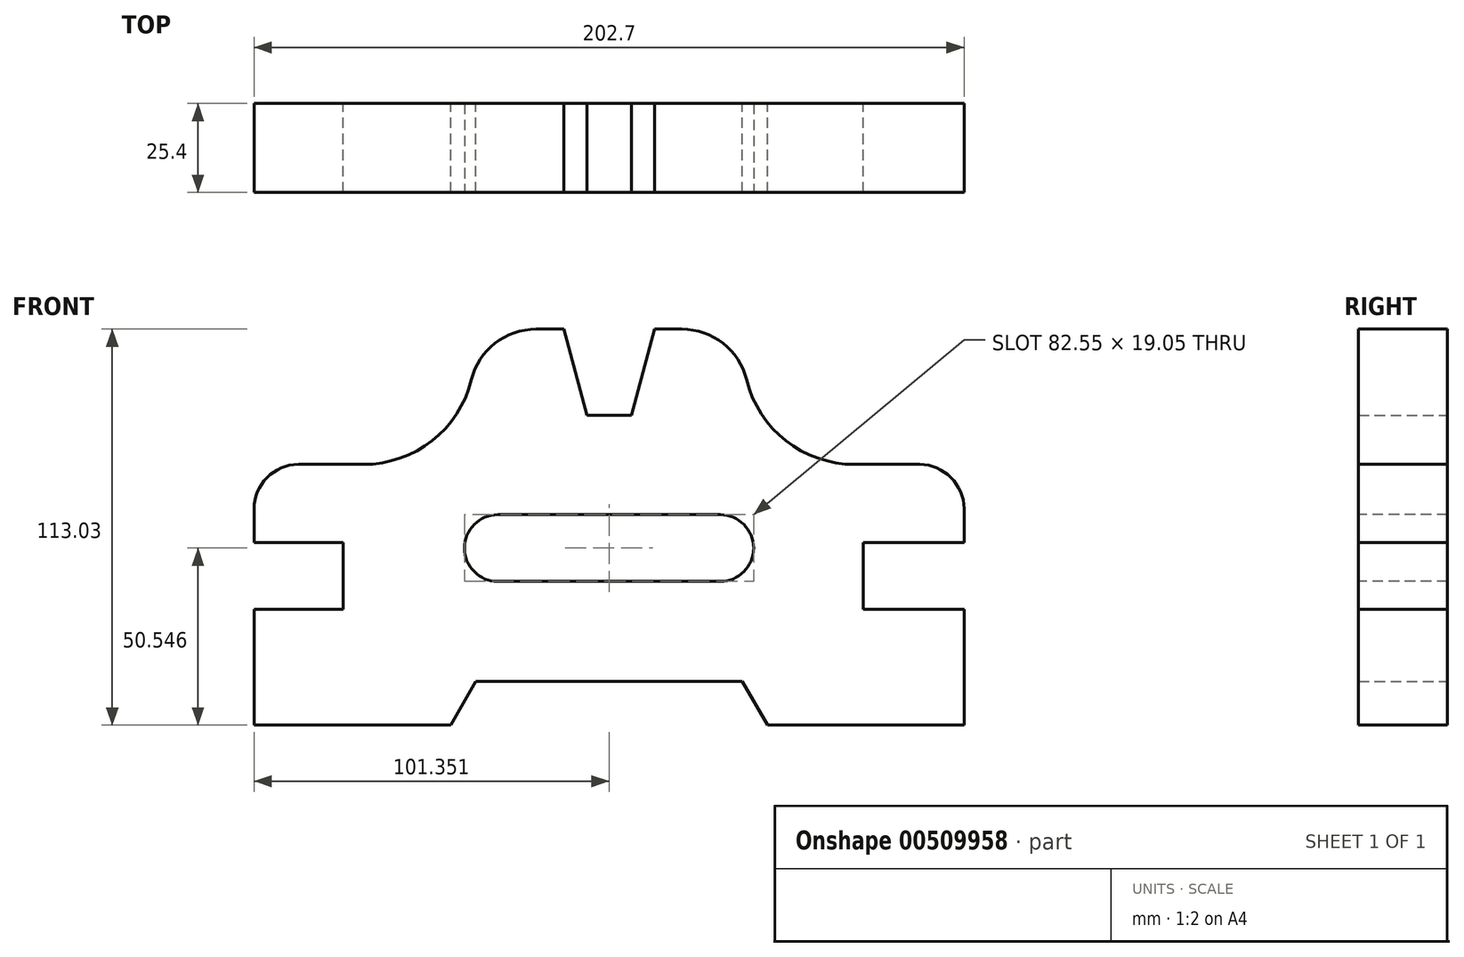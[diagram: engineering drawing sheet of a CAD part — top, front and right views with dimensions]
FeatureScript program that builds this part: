
annotation { "Feature Type Name" : "Feature", "Feature Type Description" : "" }
export const myFeature = defineFeature(function(context is Context, id is Id, definition is map)
    precondition{}
    {
        {
            var Q0;
            Q0=qCreatedBy(makeId("Front.planeOp"),FACE);
            var sketch = newSketch(context, id + "F0", { "sketchPlane" : qUnion([Q0])});
            skLineSegment(sketch, "E0", {"start": v(60.53, 19.05) * mm, "end": v(60.53, 0) * mm});
            skLineSegment(sketch, "E1", {"start": v(60.53, 0) * mm, "end": v(89.27, 0) * mm});
            skLineSegment(sketch, "E2", {"start": v(25.95, -20.57) * mm, "end": v(-50.1, -20.57) * mm});
            skLineSegment(sketch, "E3", {"start": v(-50.1, -20.57) * mm, "end": v(-57.3, -33.02) * mm});
            skLineSegment(sketch, "E4", {"start": v(-57.3, -33.02) * mm, "end": v(-113.43, -33.02) * mm});
            skLineSegment(sketch, "E5", {"start": v(-113.43, -33.02) * mm, "end": v(-113.43, 0) * mm});
            skLineSegment(sketch, "E6", {"start": v(-113.43, 0) * mm, "end": v(-113.43, 0) * mm});
            skLineSegment(sketch, "E7", {"start": v(-88.03, 19.05) * mm, "end": v(-113.43, 19.05) * mm});
            skLineSegment(sketch, "E8", {"start": v(-113.43, 19.05) * mm, "end": v(-113.43, 28.7) * mm});
            skArc(sketch, "E9", {"start": v(-113.43, 28.7) * mm, "mid": v(-109.7, 37.68) * mm, "end": v(-100.73, 41.4) * mm});
            skLineSegment(sketch, "E10", {"start": v(-100.73, 41.4) * mm, "end": v(-82.18, 41.4) * mm});
            skArc(sketch, "E11", {"start": v(-82.18, 41.4) * mm, "mid": v(-62.61, 48.15) * mm, "end": v(-51.36, 65.53) * mm});
            skArc(sketch, "E12", {"start": v(-51.36, 65.53) * mm, "mid": v(-44.61, 75.96) * mm, "end": v(-32.87, 80) * mm});
            skLineSegment(sketch, "E13", {"start": v(-32.87, 80.01) * mm, "end": v(-25.03, 80.01) * mm});
            skLineSegment(sketch, "E14", {"start": v(-12.08, 85.93) * mm, "end": v(-12.08, -61.08) * mm, "construction": true});
            skLineSegment(sketch, "E15", {"start": v(-25.03, 80.01) * mm, "end": v(-18.43, 55.37) * mm});
            skLineSegment(sketch, "E16", {"start": v(-5.73, 55.37) * mm, "end": v(-18.43, 55.37) * mm});
            skLineSegment(sketch, "E17.MirrorCS", {"start": v(89.27, 19.05) * mm, "end": v(89.27, 28.7) * mm});
            skArc(sketch, "E18.MirrorCS", {"start": v(89.27, 28.7) * mm, "mid": v(85.55, 37.68) * mm, "end": v(76.57, 41.4) * mm});
            skLineSegment(sketch, "E19.MirrorCS", {"start": v(76.57, 41.4) * mm, "end": v(58.02, 41.4) * mm});
            skArc(sketch, "E20.MirrorCS", {"start": v(58.02, 41.4) * mm, "mid": v(38.45, 48.15) * mm, "end": v(27.2, 65.53) * mm});
            skArc(sketch, "E21.MirrorCS", {"start": v(27.2, 65.53) * mm, "mid": v(20.45, 75.96) * mm, "end": v(8.7, 80) * mm});
            skLineSegment(sketch, "E22.MirrorCS", {"start": v(8.7, 80.01) * mm, "end": v(0.87, 80.01) * mm});
            skLineSegment(sketch, "E23.MirrorCS", {"start": v(0.87, 80.01) * mm, "end": v(-5.73, 55.37) * mm});
            skLineSegment(sketch, "E24.MirrorCS", {"start": v(89.27, -33.02) * mm, "end": v(89.27, 0) * mm});
            skLineSegment(sketch, "E25.MirrorCS", {"start": v(33.13, -33.02) * mm, "end": v(89.27, -33.02) * mm});
            skLineSegment(sketch, "E26", {"start": v(60.53, 19.05) * mm, "end": v(89.27, 19.05) * mm});
            skLineSegment(sketch, "E27", {"start": v(33.13, -33.02) * mm, "end": v(25.95, -20.57) * mm});
            skLineSegment(sketch, "E28", {"start": v(-5.73, 55.37) * mm, "end": v(-5.73, 67.83) * mm, "construction": true});
            skLineSegment(sketch, "E29", {"start": v(-50.1, -20.57) * mm, "end": v(-50.1, -48.1) * mm, "construction": true});
            skLineSegment(sketch, "E30", {"start": v(25.95, -20.57) * mm, "end": v(25.95, -49.1) * mm, "construction": true});
            skLineSegment(sketch, "E31", {"start": v(-88.03, 19.05) * mm, "end": v(-88.03, 0) * mm});
            skLineSegment(sketch, "E32", {"start": v(-88.03, 0) * mm, "end": v(-113.43, 0) * mm});
            skSolve(sketch);
        }
        {
            var Q0;
            Q0 = qSketchRegion(id + "F0", true);
            extrude(context, id + "F1", {"entities" : qUnion([Q0]), "depth" : 25.4 * mm, "offsetDistance" : 25.4 * mm});
        }
        {
            var Q0;
            Q0=makeQuery(id+"F1.opExtrude","CAP_FACE",FACE,{"disambiguationData":[OSD([sQuery(id+"F0.wireOp",EDGE,"E0"),sQuery(id+"F0.wireOp",EDGE,"E1"),sQuery(id+"F0.wireOp",EDGE,"E2"),sQuery(id+"F0.wireOp",EDGE,"E3"),sQuery(id+"F0.wireOp",EDGE,"E4"),sQuery(id+"F0.wireOp",EDGE,"E5"),sQuery(id+"F0.wireOp",EDGE,"E7"),sQuery(id+"F0.wireOp",EDGE,"E8"),sQuery(id+"F0.wireOp",EDGE,"E9"),sQuery(id+"F0.wireOp",EDGE,"E10"),sQuery(id+"F0.wireOp",EDGE,"E11"),sQuery(id+"F0.wireOp",EDGE,"8Uxq6lQt-N6B8-BhtL-Xwm1-FQl0PCvTUYOv"),sQuery(id+"F0.wireOp",EDGE,"E12"),sQuery(id+"F0.wireOp",EDGE,"E13"),sQuery(id+"F0.wireOp",EDGE,"E16"),sQuery(id+"F0.wireOp",EDGE,"E17.MirrorCS"),sQuery(id+"F0.wireOp",EDGE,"E18.MirrorCS"),sQuery(id+"F0.wireOp",EDGE,"E20.MirrorCS"),sQuery(id+"F0.wireOp",EDGE,"E19.MirrorCS"),sQuery(id+"F0.wireOp",EDGE,"fb8bba46-4688-4a5a-8bd3-328c5836f9c20.MirrorCS"),sQuery(id+"F0.wireOp",EDGE,"E21.MirrorCS"),sQuery(id+"F0.wireOp",EDGE,"E22.MirrorCS"),sQuery(id+"F0.wireOp",EDGE,"E23.MirrorCS"),sQuery(id+"F0.wireOp",EDGE,"E24.MirrorCS"),sQuery(id+"F0.wireOp",EDGE,"E25.MirrorCS"),sQuery(id+"F0.wireOp",EDGE,"E26"),sQuery(id+"F0.wireOp",EDGE,"E27"),sQuery(id+"F0.wireOp",EDGE,"E15"),sQuery(id+"F0.wireOp",EDGE,"E31"),sQuery(id+"F0.wireOp",EDGE,"E32")])],"isStart":false});
            var sketch = newSketch(context, id + "F2", { "sketchPlane" : qUnion([Q0])});
            skLineSegment(sketch, "E33.bottom", {"start": v(-43.83, 27.05) * mm, "end": v(19.67, 27.05) * mm});
            skLineSegment(sketch, "E33.top", {"start": v(-43.83, 8) * mm, "end": v(19.67, 8) * mm});
            skArc(sketch, "E34", {"start": v(-43.83, 27.05) * mm, "mid": v(-53.35, 17.53) * mm, "end": v(-43.83, 8) * mm});
            skArc(sketch, "E35", {"start": v(19.67, 8) * mm, "mid": v(29.2, 17.53) * mm, "end": v(19.67, 27.05) * mm});
            skSolve(sketch);
        }
        {
            var Q0;
            Q0=makeQuery(id+"F2.imprint","IMPRINT",FACE,{"disambiguationData":[TD([[makeQuery(id+"F2.imprint","IMPRINT",EDGE,{"derivedFrom":sQuery(id+"F2.wireOp",EDGE,"E33.bottom")}),-1.0]])]});
            var Q1;
            Q1 = qSketchRegion(id + "F0", true);
            extrude(context, id + "F3", {"entities" : qUnion([Q0, Q1]), "operationType" : NewBodyOperationType.REMOVE, "oppositeDirection" : true, "depth" : 25.4 * mm, "offsetDistance" : 25.4 * mm});
        }
    });
